# Revit family: Shower-Petshower-KOHLER-Spacity-K-R33033T_1
name_source: partatom
category: Plumbing Fixtures
units: mm (PartAtom-declared; Revit-internal decimal feet)

## family parameters
Cut with Voids When Loaded = No
Host = Face
OmniClass Number = 23.31.17.00
OmniClass Title = Showers
Part Type = Normal
Room Calculation Point = No
Round Connector Dimension = Use Diameter
Shared = No

## types (4) — shared parameters
ADA Compliant = No
Assembly Code = D2010700
CW Connection = No
Cold Water Inlet = Cold Water Inlet
Date Modified = 04/18/2024
Default Elevation = 72"
Description = 2F Petshower
Drain Included = No
HW Connection = Yes
Height = 12 9/16"
Hot Water Inlet = Hot Water Inlet
Length = 3 11/16"
Manufacturer = Kohler Co.
Master Format 2014 = 22 42 23
Master Format 2014 Name = Residential Showers
Material = Plastic
Pressure = 0.00 psi
Product Name = Spacity
Tempered Water Inlet = Tempered Water Inlet
URL = http://www.kohler.com.cn
Vent Connection = No
Waste Connection = No
Waste Water Outlet = Waste Water Outlet
WaterSense Certified = No
Width = 2 1/4"

## per-type parameters (varying)
| type | Clip Finish | Faceplate Finish | Finish | Flow Rate | Model | Type |
| 1.75 GPM, BPT-Black | Plastic-Pantone-Black_C | Plastic-Pantone-PQ-194205-TCX | Kohler-Plastic-BPT-Black | 2 GPM | K-R33033T-G-BPT | 1 |
| 1.75 GPM, WPT-White | Plastic-Pantone-PQ-11-4800-TCX | Kohler-Plastic-NY-Dune | Kohler-Plastic-WPT-White | 2 GPM | K-R33033T-G-WPT | 2 |
| 2.5 GPM, BPT-Black | Plastic-Pantone-Black_C | Plastic-Pantone-PQ-194205-TCX | Kohler-Plastic-BPT-Black | 3 GPM | K-R33033T-BPT | 3 |
| 2.5 GPM, WPT-White | Plastic-Pantone-PQ-11-4800-TCX | Kohler-Plastic-NY-Dune | Kohler-Plastic-WPT-White | 3 GPM | K-R33033T-WPT | 4 |

## geometry (parser evidence)
native form markers: Sweep x6
no freeform markers — native parametric forms only
